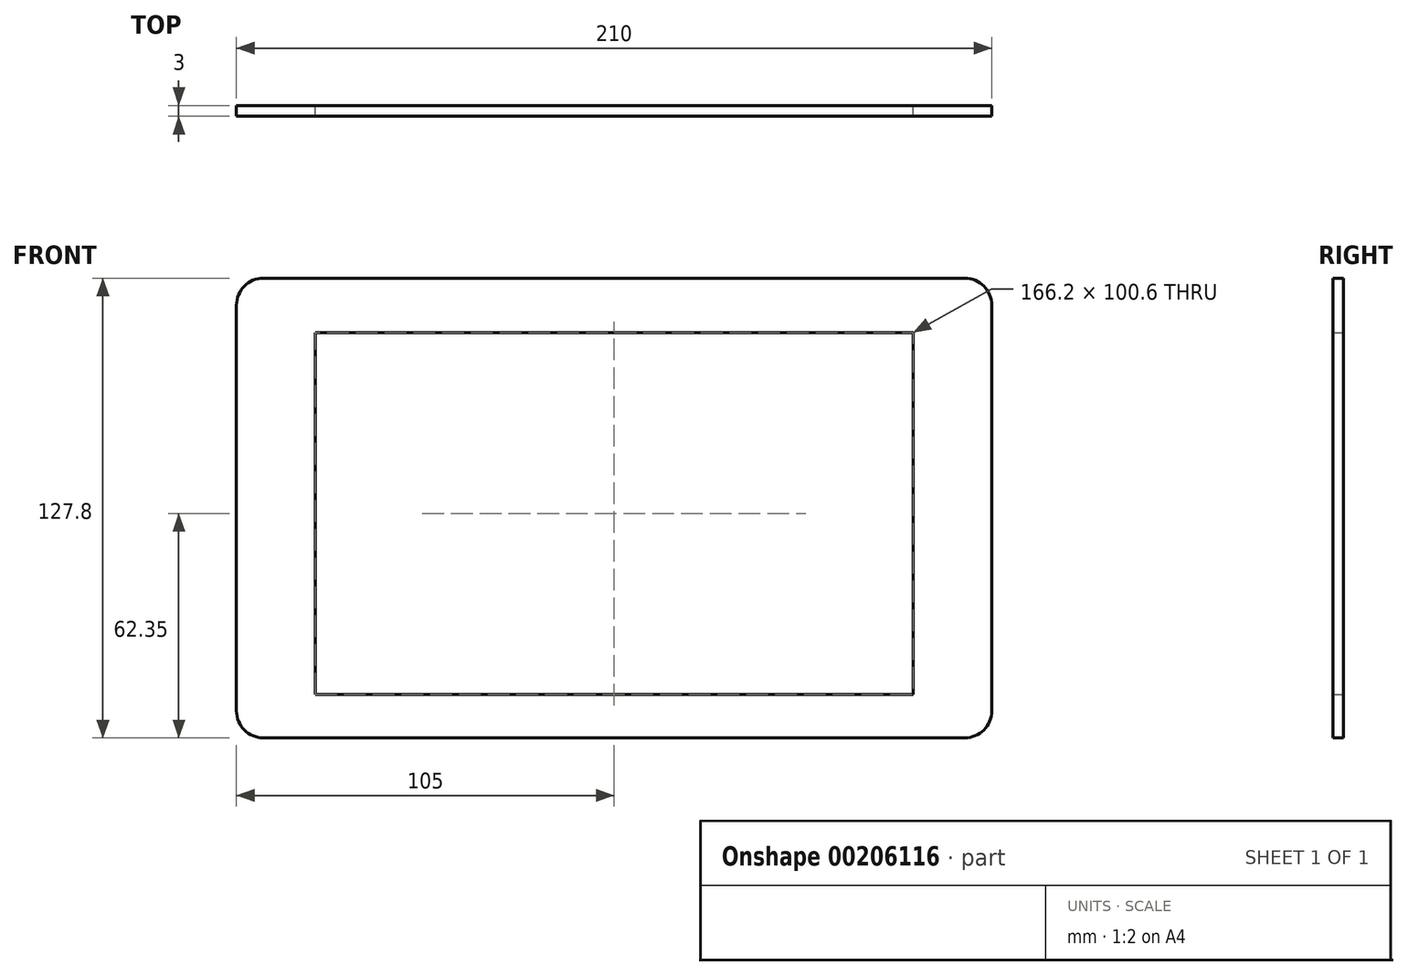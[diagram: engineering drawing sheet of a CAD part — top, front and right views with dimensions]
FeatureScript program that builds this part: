
annotation { "Feature Type Name" : "Feature", "Feature Type Description" : "" }
export const myFeature = defineFeature(function(context is Context, id is Id, definition is map)
    precondition{}
    {
        {
            var Q0;
            Q0=qCreatedBy(makeId("Front.planeOp"),FACE);
            var sketch = newSketch(context, id + "F0", { "sketchPlane" : qUnion([Q0])});
            skPoint(sketch, "E0.middle", {"position": v(0, 0) * mm});
            skLineSegment(sketch, "E1.bottom", {"start": v(97.5, 63.9) * mm, "end": v(-97.5, 63.9) * mm});
            skLineSegment(sketch, "E1.top", {"start": v(97.5, -63.9) * mm, "end": v(-97.5, -63.9) * mm});
            skLineSegment(sketch, "E1.left", {"start": v(105, 56.4) * mm, "end": v(105, -56.4) * mm});
            skLineSegment(sketch, "E1.right", {"start": v(-105, 56.4) * mm, "end": v(-105, -56.4) * mm});
            skPoint(sketch, "E2.visualSharp", {"position": v(-105, -63.9) * mm});
            skArc(sketch, "E2.filletArc", {"start": v(-105, -56.4) * mm, "mid": v(-102.8, -61.7) * mm, "end": v(-97.5, -63.9) * mm});
            skPoint(sketch, "E3.visualSharp", {"position": v(105, -63.9) * mm});
            skArc(sketch, "E3.filletArc", {"start": v(97.5, -63.9) * mm, "mid": v(102.8, -61.7) * mm, "end": v(105, -56.4) * mm});
            skPoint(sketch, "E4.visualSharp", {"position": v(105, 63.9) * mm});
            skArc(sketch, "E4.filletArc", {"start": v(105, 56.4) * mm, "mid": v(102.8, 61.7) * mm, "end": v(97.5, 63.9) * mm});
            skPoint(sketch, "E5.visualSharp", {"position": v(-105, 63.9) * mm});
            skArc(sketch, "E5.filletArc", {"start": v(-97.5, 63.9) * mm, "mid": v(-102.8, 61.7) * mm, "end": v(-105, 56.4) * mm});
            skLineSegment(sketch, "E6", {"start": v(0, 55.38) * mm, "end": v(0, 48.75) * mm, "construction": true});
            skPoint(sketch, "E6.endSnap0", {"position": v(0, 55.38) * mm});
            skLineSegment(sketch, "E7", {"start": v(0, 48.75) * mm, "end": v(0, -51.85) * mm, "construction": true});
            skPoint(sketch, "E7.endSnap0", {"position": v(0, -55.38) * mm});
            skLineSegment(sketch, "E8.bottom", {"start": v(83.1, 48.75) * mm, "end": v(-83.1, 48.75) * mm, "construction": true});
            skLineSegment(sketch, "E8.top", {"start": v(83.1, -51.85) * mm, "end": v(-83.1, -51.85) * mm, "construction": true});
            skLineSegment(sketch, "E8.left", {"start": v(83.1, 48.75) * mm, "end": v(83.1, -51.85) * mm, "construction": true});
            skLineSegment(sketch, "E8.right", {"start": v(-83.1, 48.75) * mm, "end": v(-83.1, -51.85) * mm, "construction": true});
            skPoint(sketch, "E8.middle", {"position": v(0, -1.55) * mm});
            skLineSegment(sketch, "E9.bottom", {"start": v(-83.1, 48.75) * mm, "end": v(83.1, 48.75) * mm});
            skLineSegment(sketch, "E9.top", {"start": v(-83.1, -51.85) * mm, "end": v(83.1, -51.85) * mm});
            skLineSegment(sketch, "E9.left", {"start": v(-83.1, 48.75) * mm, "end": v(-83.1, -51.85) * mm});
            skLineSegment(sketch, "E9.right", {"start": v(83.1, 48.75) * mm, "end": v(83.1, -51.85) * mm});
            skPoint(sketch, "E0.left.end.orphan", {"position": v(96.48, 55.38) * mm});
            skPoint(sketch, "E10.orphan", {"position": v(96.48, -55.38) * mm});
            skPoint(sketch, "E0.right.end.orphan", {"position": v(-96.48, 55.38) * mm});
            skPoint(sketch, "E0.right.start.orphan", {"position": v(-96.48, -55.38) * mm});
            skSolve(sketch);
        }
        {
            var Q0;
            Q0=makeQuery(id+"F0.imprint","IMPRINT",FACE,{"disambiguationData":[TD([[makeQuery(id+"F0.imprint","IMPRINT",EDGE,{"derivedFrom":sQuery(id+"F0.wireOp",EDGE,"E0.bottom")}),1.0]])]});
            var Q1;
            Q1=makeQuery(id+"F0.imprint","IMPRINT",FACE,{"disambiguationData":[TD([[makeQuery(id+"F0.imprint","IMPRINT",EDGE,{"derivedFrom":sQuery(id+"F0.wireOp",EDGE,"E0.bottom")}),-1.0]])]});
            var Q2;
            Q2=makeQuery(id+"F0.imprint","IMPRINT",FACE,{"disambiguationData":[TD([[makeQuery(id+"F0.imprint","IMPRINT",EDGE,{"derivedFrom":sQuery(id+"F0.wireOp",EDGE,"E1.bottom")}),1.0]])]});
            extrude(context, id + "F1", {"entities" : qUnion([Q0, Q1, Q2]), "depth" : 3 * mm});
        }
    });
